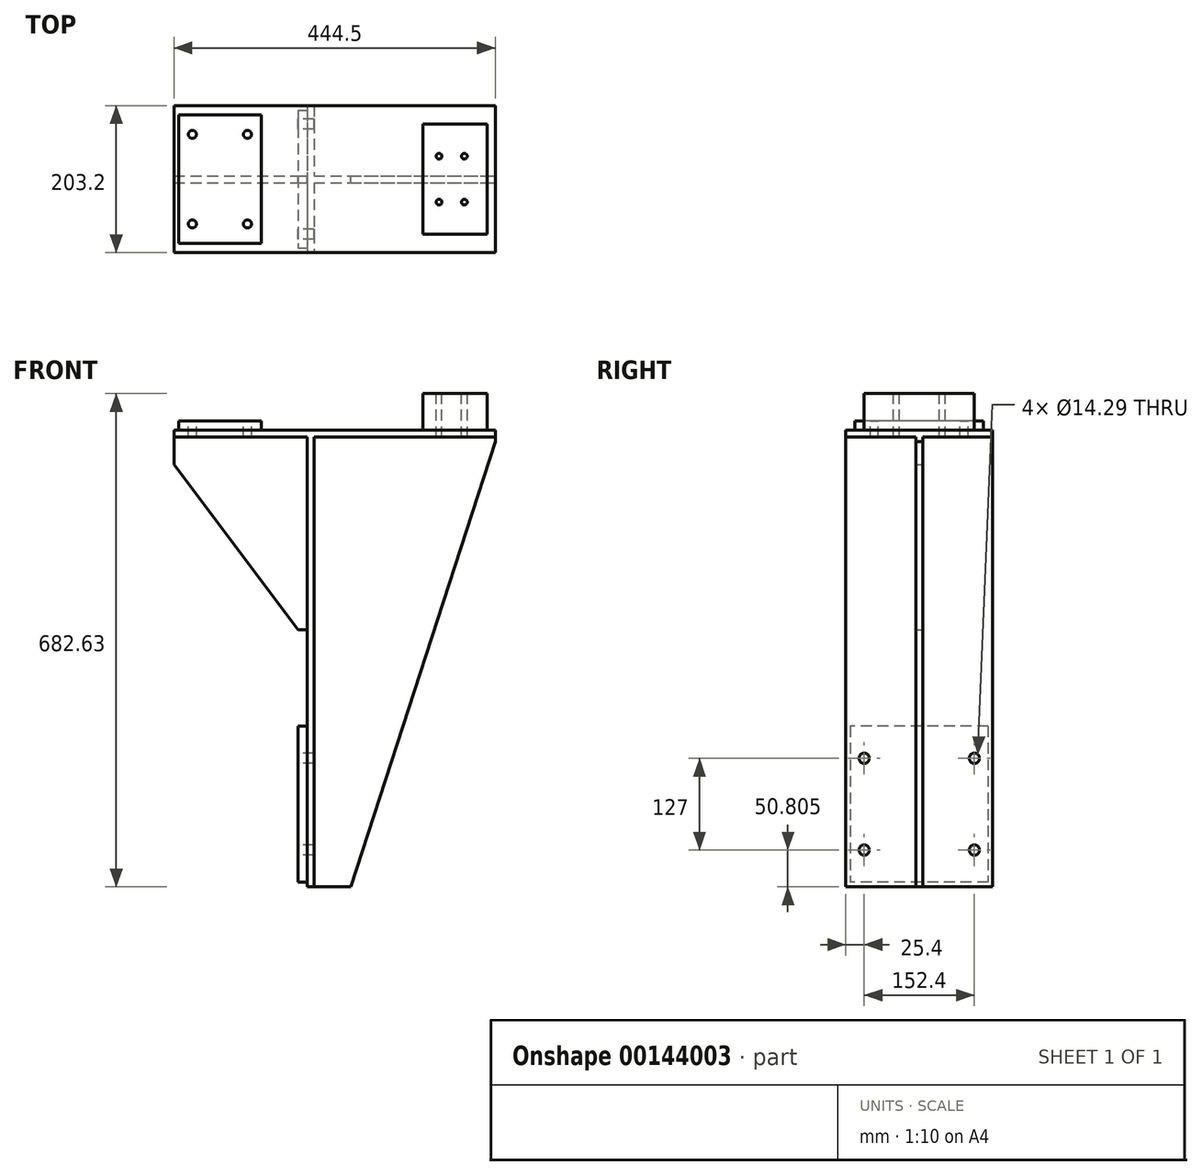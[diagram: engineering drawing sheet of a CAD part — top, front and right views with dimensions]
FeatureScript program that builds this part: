
annotation { "Feature Type Name" : "Feature", "Feature Type Description" : "" }
export const myFeature = defineFeature(function(context is Context, id is Id, definition is map)
    precondition{}
    {
        {
            var Q0;
            Q0=qCreatedBy(makeId("Top.planeOp"),FACE);
            var sketch = newSketch(context, id + "F0", { "sketchPlane" : qUnion([Q0])});
            skLineSegment(sketch, "E0.rect.bottom", {"start": v(-222.25, 101.6) * mm, "end": v(222.25, 101.6) * mm});
            skLineSegment(sketch, "E0.rect.top", {"start": v(-222.25, -101.6) * mm, "end": v(222.25, -101.6) * mm});
            skLineSegment(sketch, "E0.rect.left", {"start": v(-222.25, 101.6) * mm, "end": v(-222.25, -101.6) * mm});
            skLineSegment(sketch, "E0.rect.right", {"start": v(222.25, 101.6) * mm, "end": v(222.25, -101.6) * mm});
            skPoint(sketch, "E0.rect.middle", {"position": v(0, 0) * mm});
            skSolve(sketch);
        }
        {
            var Q0;
            Q0=qSketchRegion(id+"F0",true);
            extrude(context, id + "F1", {"entities" : qUnion([Q0]), "oppositeDirection" : true, "depth" : 9.52 * mm});
        }
        {
            var Q0;
            Q0=makeQuery(id+"F1.opExtrude","CAP_FACE",FACE,{"disambiguationData":[OSD([sQuery(id+"F0.wireOp",EDGE,"E0.rect.bottom"),sQuery(id+"F0.wireOp",EDGE,"E0.rect.top"),sQuery(id+"F0.wireOp",EDGE,"E0.rect.left"),sQuery(id+"F0.wireOp",EDGE,"E0.rect.right")])],"isStart":true});
            var sketch = newSketch(context, id + "F2", { "sketchPlane" : qUnion([Q0])});
            skLineSegment(sketch, "E1.0", {"start": v(-158.75, 101.6) * mm, "end": v(-158.75, -101.6) * mm, "construction": true});
            skLineSegment(sketch, "E2.0", {"start": v(-215.9, 101.6) * mm, "end": v(-215.9, -101.6) * mm, "construction": true});
            skLineSegment(sketch, "E3.MirrorCS", {"start": v(-101.6, 101.6) * mm, "end": v(-101.6, -101.6) * mm, "construction": true});
            skLineSegment(sketch, "E4", {"start": v(-247.12, 0) * mm, "end": v(246.46, 0) * mm, "construction": true});
            skLineSegment(sketch, "E5.0", {"start": v(-247.12, 88.9) * mm, "end": v(246.46, 88.9) * mm, "construction": true});
            skLineSegment(sketch, "E6.MirrorCS", {"start": v(-247.12, -88.9) * mm, "end": v(246.46, -88.9) * mm, "construction": true});
            skLineSegment(sketch, "E7.bottom", {"start": v(-215.9, 88.9) * mm, "end": v(-101.6, 88.9) * mm});
            skLineSegment(sketch, "E7.top", {"start": v(-215.9, -88.9) * mm, "end": v(-101.6, -88.9) * mm});
            skLineSegment(sketch, "E7.left", {"start": v(-215.9, 88.9) * mm, "end": v(-215.9, -88.9) * mm});
            skLineSegment(sketch, "E7.right", {"start": v(-101.6, 88.9) * mm, "end": v(-101.6, -88.9) * mm});
            skSolve(sketch);
        }
        {
            var Q0;
            Q0=qSketchRegion(id+"F2",true);
            extrude(context, id + "F3", {"entities" : qUnion([Q0]), "operationType" : NewBodyOperationType.ADD, "depth" : 12.7 * mm});
        }
        {
            var Q0;
            Q0=makeQuery(id+"F3.opExtrude","CAP_FACE",FACE,{"disambiguationData":[OSD([sQuery(id+"F2.wireOp",EDGE,"E7.bottom"),sQuery(id+"F2.wireOp",EDGE,"E7.top"),sQuery(id+"F2.wireOp",EDGE,"E7.left"),sQuery(id+"F2.wireOp",EDGE,"E7.right")])],"isStart":false});
            var sketch = newSketch(context, id + "F4", { "sketchPlane" : qUnion([Q0])});
            skLineSegment(sketch, "E8", {"start": v(-158.75, 88.9) * mm, "end": v(-158.75, -88.9) * mm, "construction": true});
            skLineSegment(sketch, "E9", {"start": v(-215.9, 0) * mm, "end": v(-101.6, 0) * mm, "construction": true});
            skLineSegment(sketch, "E10.0", {"start": v(-215.9, 61.98) * mm, "end": v(-101.6, 61.98) * mm, "construction": true});
            skLineSegment(sketch, "E11.0", {"start": v(-196.85, 88.9) * mm, "end": v(-196.85, -88.9) * mm, "construction": true});
            skPoint(sketch, "E12", {"position": v(-196.85, 61.98) * mm});
            skPoint(sketch, "E13.MirrorP", {"position": v(-120.65, 61.98) * mm});
            skPoint(sketch, "E14.MirrorP", {"position": v(-120.65, -61.98) * mm});
            skPoint(sketch, "E15.MirrorP", {"position": v(-196.85, -61.98) * mm});
            skSolve(sketch);
        }
        {
            var Q0;
            Q0=sQuery(id+"F4.wireOp",VERTEX,"E12");
            var Q1;
            Q1=sQuery(id+"F4.wireOp",VERTEX,"E13.MirrorP");
            var Q2;
            Q2=sQuery(id+"F4.wireOp",VERTEX,"E15.MirrorP");
            var Q3;
            Q3=sQuery(id+"F4.wireOp",VERTEX,"E14.MirrorP");
            var Q4;
            Q4=makeQuery(id+"F1.opExtrude","SWEPT_BODY",BODY,{"disambiguationData":[OSD([sQuery(id+"F0.wireOp",EDGE,"E0.rect.bottom"),sQuery(id+"F0.wireOp",EDGE,"E0.rect.top"),sQuery(id+"F0.wireOp",EDGE,"E0.rect.left"),sQuery(id+"F0.wireOp",EDGE,"E0.rect.right")])]});
            hole(context, id + "F5", {"style" : HoleStyle.SIMPLE, "holeDiameter" : 11.1 * mm, "endStyle" : HoleEndStyle.THROUGH, "locations" : qUnion([Q0, Q1, Q2, Q3]), "scope" : qUnion([Q4])});
        }
        {
            var Q0;
            Q0=makeQuery(id+"F1.opExtrude","CAP_FACE",FACE,{"disambiguationData":[OSD([sQuery(id+"F0.wireOp",EDGE,"E0.rect.bottom"),sQuery(id+"F0.wireOp",EDGE,"E0.rect.top"),sQuery(id+"F0.wireOp",EDGE,"E0.rect.left"),sQuery(id+"F0.wireOp",EDGE,"E0.rect.right")])],"isStart":true});
            var sketch = newSketch(context, id + "F6", { "sketchPlane" : qUnion([Q0])});
            skLineSegment(sketch, "E16.0", {"start": v(-215.9, -88.9) * mm, "end": v(-101.6, -88.9) * mm, "construction": true});
            skLineSegment(sketch, "E17", {"start": v(-158.75, -88.9) * mm, "end": v(-158.75, 123.27) * mm, "construction": true});
            skLineSegment(sketch, "E18.0", {"start": v(161.93, -88.9) * mm, "end": v(161.92, 123.27) * mm, "construction": true});
            skLineSegment(sketch, "E19.0", {"start": v(122.3, -88.9) * mm, "end": v(122.3, 123.27) * mm, "construction": true});
            skLineSegment(sketch, "E20.0", {"start": v(211.2, -88.9) * mm, "end": v(211.2, 123.27) * mm, "construction": true});
            skLineSegment(sketch, "E21.0", {"start": v(-222.25, 101.6) * mm, "end": v(-222.25, -101.6) * mm, "construction": true});
            skLineSegment(sketch, "E22", {"start": v(-222.25, 0) * mm, "end": v(238.55, 0) * mm, "construction": true});
            skLineSegment(sketch, "E23.0", {"start": v(-222.25, 76.2) * mm, "end": v(238.55, 76.2) * mm, "construction": true});
            skLineSegment(sketch, "E24.bottom", {"start": v(122.3, 76.2) * mm, "end": v(211.2, 76.2) * mm});
            skLineSegment(sketch, "E24.top", {"start": v(122.3, -76.2) * mm, "end": v(211.2, -76.2) * mm});
            skLineSegment(sketch, "E24.left", {"start": v(122.3, 76.2) * mm, "end": v(122.3, -76.2) * mm});
            skLineSegment(sketch, "E24.right", {"start": v(211.2, 76.2) * mm, "end": v(211.2, -76.2) * mm});
            skSolve(sketch);
        }
        {
            var Q0;
            Q0=qSketchRegion(id+"F6",true);
            extrude(context, id + "F7", {"entities" : qUnion([Q0]), "operationType" : NewBodyOperationType.ADD, "depth" : 50.8 * mm});
        }
        {
            var Q0;
            Q0=makeQuery(id+"F7.opExtrude","CAP_FACE",FACE,{"disambiguationData":[OSD([sQuery(id+"F6.wireOp",EDGE,"E24.bottom"),sQuery(id+"F6.wireOp",EDGE,"E24.top"),sQuery(id+"F6.wireOp",EDGE,"E24.left"),sQuery(id+"F6.wireOp",EDGE,"E24.right")])],"isStart":false});
            var sketch = newSketch(context, id + "F8", { "sketchPlane" : qUnion([Q0])});
            skLineSegment(sketch, "E25.0", {"start": v(161.93, -88.9) * mm, "end": v(161.92, 123.27) * mm, "construction": true});
            skLineSegment(sketch, "E26.0", {"start": v(144.4, -88.9) * mm, "end": v(144.4, 123.27) * mm, "construction": true});
            skLineSegment(sketch, "E27.0", {"start": v(-222.25, 0) * mm, "end": v(238.55, 0) * mm, "construction": true});
            skLineSegment(sketch, "E28.0", {"start": v(-222.25, 31.75) * mm, "end": v(238.55, 31.75) * mm, "construction": true});
            skPoint(sketch, "E29", {"position": v(144.4, 31.75) * mm});
            skPoint(sketch, "E30.MirrorP", {"position": v(179.45, 31.75) * mm});
            skPoint(sketch, "E31.MirrorP", {"position": v(144.4, -31.75) * mm});
            skPoint(sketch, "E32.MirrorP", {"position": v(179.45, -31.75) * mm});
            skSolve(sketch);
        }
        {
            var Q0;
            Q0=sQuery(id+"F8.wireOp",VERTEX,"E29");
            var Q1;
            Q1=sQuery(id+"F8.wireOp",VERTEX,"E30.MirrorP");
            var Q2;
            Q2=sQuery(id+"F8.wireOp",VERTEX,"E31.MirrorP");
            var Q3;
            Q3=sQuery(id+"F8.wireOp",VERTEX,"E32.MirrorP");
            var Q4;
            Q4=makeQuery(id+"F1.opExtrude","SWEPT_BODY",BODY,{"disambiguationData":[OSD([sQuery(id+"F0.wireOp",EDGE,"E0.rect.bottom"),sQuery(id+"F0.wireOp",EDGE,"E0.rect.top"),sQuery(id+"F0.wireOp",EDGE,"E0.rect.left"),sQuery(id+"F0.wireOp",EDGE,"E0.rect.right")])]});
            hole(context, id + "F9", {"style" : HoleStyle.SIMPLE, "holeDiameter" : 7.94 * mm, "endStyle" : HoleEndStyle.THROUGH, "locations" : qUnion([Q0, Q1, Q2, Q3]), "scope" : qUnion([Q4])});
        }
        {
            var Q0;
            Q0=makeQuery(id+"F1.opExtrude","SWEPT_FACE",FACE,{"disambiguationData":[OSD([sQuery(id+"F0.wireOp",EDGE,"E0.rect.left")])]});
            cPlane(context, id + "F10", {"entities" : qUnion([Q0]), "cplaneType" : CPlaneType.OFFSET, "offset" : 184.15 * mm, "oppositeDirection" : true, "width" : 152.4 * mm, "height" : 152.4 * mm});
        }
        {
            var Q0;
            Q0=qCreatedBy(id+"F10.planeOp",FACE);
            var sketch = newSketch(context, id + "F11", { "sketchPlane" : qUnion([Q0])});
            skLineSegment(sketch, "E33.0", {"start": v(-101.6, -9.53) * mm, "end": v(101.6, -9.53) * mm});
            skLineSegment(sketch, "E34.0", {"start": v(-101.6, -631.83) * mm, "end": v(101.6, -631.83) * mm});
            skLineSegment(sketch, "E35", {"start": v(-101.6, -9.53) * mm, "end": v(-101.6, -631.83) * mm});
            skLineSegment(sketch, "E36", {"start": v(101.6, -9.53) * mm, "end": v(101.6, -631.83) * mm});
            skSolve(sketch);
        }
        {
            var Q0;
            Q0=qSketchRegion(id+"F11",true);
            extrude(context, id + "F12", {"entities" : qUnion([Q0]), "operationType" : NewBodyOperationType.ADD, "oppositeDirection" : true, "depth" : 9.52 * mm});
        }
        {
            var Q0;
            Q0=qCreatedBy(makeId("Front.planeOp"),FACE);
            var sketch = newSketch(context, id + "F13", { "sketchPlane" : qUnion([Q0])});
            skLineSegment(sketch, "E37.0", {"start": v(-222.25, -9.53) * mm, "end": v(-38.1, -9.53) * mm});
            skLineSegment(sketch, "E38.0", {"start": v(-38.1, -9.53) * mm, "end": v(-38.1, -631.83) * mm});
            skLineSegment(sketch, "E39", {"start": v(-222.25, -9.52) * mm, "end": v(-222.25, -47.63) * mm});
            skLineSegment(sketch, "E40", {"start": v(-222.25, -47.62) * mm, "end": v(-50.8, -276.23) * mm});
            skLineSegment(sketch, "E41", {"start": v(-50.8, -276.23) * mm, "end": v(-38.1, -276.23) * mm});
            skSolve(sketch);
        }
        {
            var Q0;
            Q0=qSketchRegion(id+"F13",true);
            extrude(context, id + "F14", {"entities" : qUnion([Q0]), "operationType" : NewBodyOperationType.ADD, "endBound" : BoundingType.SYMMETRIC, "depth" : 9.52 * mm});
        }
        {
            var Q0;
            Q0=qCreatedBy(makeId("Front.planeOp"),FACE);
            var sketch = newSketch(context, id + "F15", { "sketchPlane" : qUnion([Q0])});
            skLineSegment(sketch, "E42.0", {"start": v(-28.58, -9.53) * mm, "end": v(222.25, -9.53) * mm});
            skLineSegment(sketch, "E43.0", {"start": v(-28.58, -9.53) * mm, "end": v(-28.58, -631.83) * mm});
            skLineSegment(sketch, "E44", {"start": v(-28.58, -631.83) * mm, "end": v(22.22, -631.83) * mm});
            skLineSegment(sketch, "E45", {"start": v(22.22, -631.83) * mm, "end": v(222.25, -15.87) * mm});
            skLineSegment(sketch, "E46", {"start": v(222.25, -15.88) * mm, "end": v(222.25, -9.52) * mm});
            skSolve(sketch);
        }
        {
            var Q0;
            Q0=qSketchRegion(id+"F15",true);
            extrude(context, id + "F16", {"entities" : qUnion([Q0]), "operationType" : NewBodyOperationType.ADD, "endBound" : BoundingType.SYMMETRIC, "depth" : 9.52 * mm});
        }
        {
            var Q0;
            Q0=makeQuery(id+"F12.opExtrude","CAP_FACE",FACE,{"disambiguationData":[OSD([sQuery(id+"F11.wireOp",EDGE,"E33.0"),sQuery(id+"F11.wireOp",EDGE,"E34.0"),sQuery(id+"F11.wireOp",EDGE,"E35"),sQuery(id+"F11.wireOp",EDGE,"E36")])],"isStart":true});
            var sketch = newSketch(context, id + "F17", { "sketchPlane" : qUnion([Q0])});
            skLineSegment(sketch, "E47.0", {"start": v(-101.6, -9.53) * mm, "end": v(-101.6, -631.83) * mm, "construction": true});
            skLineSegment(sketch, "E48.0", {"start": v(-101.6, -631.83) * mm, "end": v(101.6, -631.83) * mm, "construction": true});
            skLineSegment(sketch, "E49.0", {"start": v(101.6, -9.53) * mm, "end": v(101.6, -631.83) * mm, "construction": true});
            skLineSegment(sketch, "E50.0", {"start": v(-101.6, -625.48) * mm, "end": v(101.6, -625.48) * mm, "construction": true});
            skLineSegment(sketch, "E51.0", {"start": v(-101.6, -409.58) * mm, "end": v(101.6, -409.58) * mm, "construction": true});
            skLineSegment(sketch, "E52.0", {"start": v(-95.25, -9.53) * mm, "end": v(-95.25, -631.83) * mm, "construction": true});
            skLineSegment(sketch, "E53.bottom", {"start": v(-95.25, -409.58) * mm, "end": v(95.25, -409.58) * mm});
            skLineSegment(sketch, "E53.top", {"start": v(-95.25, -625.48) * mm, "end": v(95.25, -625.48) * mm});
            skLineSegment(sketch, "E53.left", {"start": v(-95.25, -409.58) * mm, "end": v(-95.25, -625.48) * mm});
            skLineSegment(sketch, "E53.right", {"start": v(95.25, -409.58) * mm, "end": v(95.25, -625.48) * mm});
            skSolve(sketch);
        }
        {
            var Q0;
            Q0=qSketchRegion(id+"F17",true);
            extrude(context, id + "F18", {"entities" : qUnion([Q0]), "operationType" : NewBodyOperationType.ADD, "depth" : 12.7 * mm});
        }
        {
            var Q0;
            Q0=makeQuery(id+"F18.opExtrude","CAP_FACE",FACE,{"disambiguationData":[OSD([sQuery(id+"F17.wireOp",EDGE,"E53.bottom"),sQuery(id+"F17.wireOp",EDGE,"E53.top"),sQuery(id+"F17.wireOp",EDGE,"E53.left"),sQuery(id+"F17.wireOp",EDGE,"E53.right")])],"isStart":false});
            var sketch = newSketch(context, id + "F19", { "sketchPlane" : qUnion([Q0])});
            skLineSegment(sketch, "E54.0", {"start": v(-95.25, -409.58) * mm, "end": v(95.25, -409.58) * mm, "construction": true});
            skLineSegment(sketch, "E55", {"start": v(0, -454.03) * mm, "end": v(0, -581.03) * mm, "construction": true});
            skPoint(sketch, "E55.endSnap0", {"position": v(0, -625.48) * mm});
            skLineSegment(sketch, "E56.0", {"start": v(-95.25, -454.03) * mm, "end": v(95.25, -454.03) * mm, "construction": true});
            skLineSegment(sketch, "E57.0", {"start": v(-95.25, -581.03) * mm, "end": v(95.25, -581.03) * mm, "construction": true});
            skLineSegment(sketch, "E58.0", {"start": v(-76.2, -409.58) * mm, "end": v(-76.2, -650.06) * mm, "construction": true});
            skPoint(sketch, "E59.orphan", {"position": v(0, -409.58) * mm});
            skPoint(sketch, "E60.trimOffspring.end.orphan", {"position": v(0, -650.06) * mm});
            skLineSegment(sketch, "E61", {"start": v(0, -517.53) * mm, "end": v(-162.58, -517.53) * mm, "construction": true});
            skPoint(sketch, "E62", {"position": v(-76.2, -454.03) * mm});
            skPoint(sketch, "E63", {"position": v(-76.2, -581.03) * mm});
            skPoint(sketch, "E64.MirrorP", {"position": v(76.2, -454.03) * mm});
            skPoint(sketch, "E65.MirrorP", {"position": v(76.2, -581.03) * mm});
            skSolve(sketch);
        }
        {
            var Q0;
            Q0=sQuery(id+"F19.wireOp",VERTEX,"E62");
            var Q1;
            Q1=sQuery(id+"F19.wireOp",VERTEX,"E64.MirrorP");
            var Q2;
            Q2=sQuery(id+"F19.wireOp",VERTEX,"E63");
            var Q3;
            Q3=sQuery(id+"F19.wireOp",VERTEX,"E65.MirrorP");
            var Q4;
            Q4=makeQuery(id+"F1.opExtrude","SWEPT_BODY",BODY,{"disambiguationData":[OSD([sQuery(id+"F0.wireOp",EDGE,"E0.rect.bottom"),sQuery(id+"F0.wireOp",EDGE,"E0.rect.top"),sQuery(id+"F0.wireOp",EDGE,"E0.rect.left"),sQuery(id+"F0.wireOp",EDGE,"E0.rect.right")])]});
            hole(context, id + "F20", {"style" : HoleStyle.SIMPLE, "holeDiameter" : 14.29 * mm, "endStyle" : HoleEndStyle.THROUGH, "locations" : qUnion([Q0, Q1, Q2, Q3]), "scope" : qUnion([Q4])});
        }
    });
